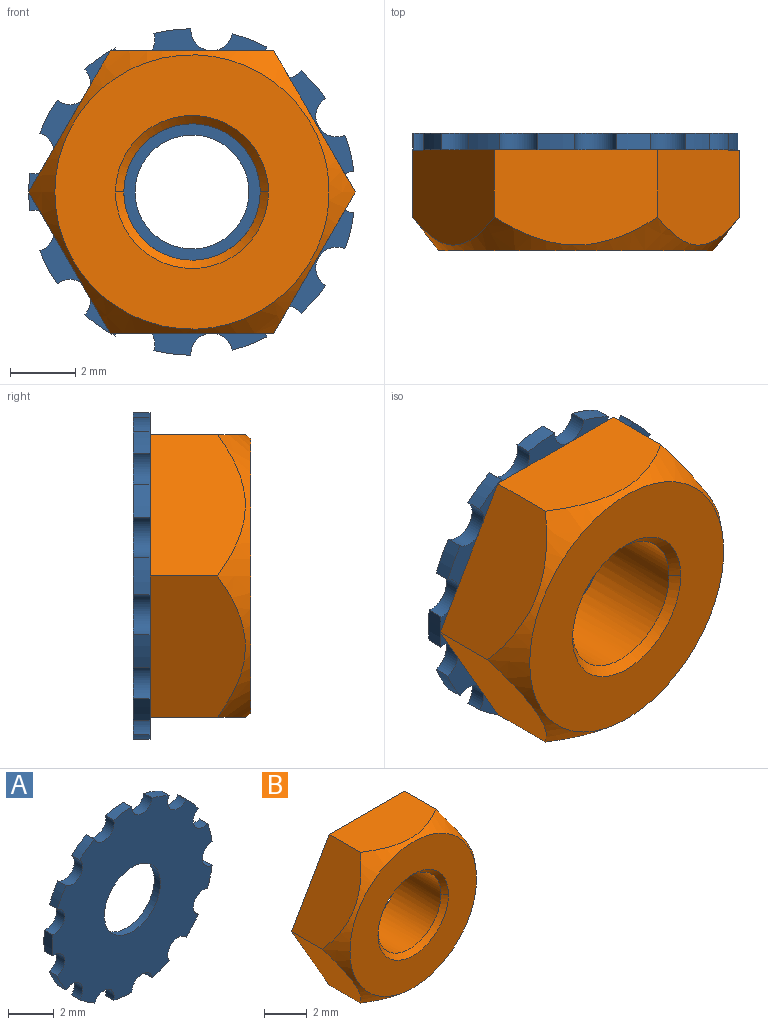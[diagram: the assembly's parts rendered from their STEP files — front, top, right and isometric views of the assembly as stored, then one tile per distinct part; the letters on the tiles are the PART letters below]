
ASSEMBLY  parts=2 mates=1
PART A: 31 faces, bbox 9.9x0.5x10 mm
  f0: cylinder r=4.99mm len=1.13mm, axis (0,1,0), area 0.6mm2, adj f1,f2,f3,f4
  f1: cylinder r=0.64mm len=1.26mm, axis (0,1,0), area 1mm2, adj f0,f2,f4,f19
  f2: plane 9.97x9.93mm, normal (0,1,0), area 43.3mm2, adj f0,f1,f3,f5,f6,f7,f8,f9
  f3: cylinder r=0.64mm len=1.21mm, axis (0,1,0), area 1mm2, adj f0,f2,f4,f15
  f4: plane 9.97x9.93mm, normal (0,-1,0), area 60.6mm2, adj f0,f1,f3,f5,f6,f7,f8,f9
  f5: cylinder r=4.99mm len=1.14mm, axis (0,1,0), area 0.6mm2, adj f2,f4,f23,f24
  f6: cylinder r=0.64mm len=1.27mm, axis (0,1,0), area 1mm2, adj f2,f4,f21,f25
  f7: cylinder r=4.99mm len=1.06mm, axis (0,1,0), area 0.6mm2, adj f2,f4,f12,f20
  f8: cylinder r=4.99mm len=0.85mm, axis (0,1,0), area 0.6mm2, adj f2,f4,f9,f16
  f9: cylinder r=0.64mm len=1.18mm, axis (0,1,0), area 1mm2, adj f2,f4,f8,f25
  f10: cylinder r=2.92mm len=5.84mm, axis (0,1,0), area 2.3mm2, adj f2,f30
  f11: cylinder r=4.99mm len=1.01mm, axis (0,1,0), area 0.6mm2, adj f2,f4,f23,f28
  f12: cylinder r=0.64mm len=1.13mm, axis (0,1,0), area 1mm2, adj f2,f4,f7,f14
  f13: cylinder r=0.64mm len=1.18mm, axis (0,1,0), area 1mm2, adj f2,f4,f14,f21
  f14: cylinder r=4.99mm len=0.85mm, axis (0,1,0), area 0.6mm2, adj f2,f4,f12,f13
  f15: cylinder r=4.99mm len=0.94mm, axis (0,1,0), area 0.6mm2, adj f2,f3,f4,f28
  f16: cylinder r=0.64mm len=1.13mm, axis (0,1,0), area 1mm2, adj f2,f4,f8,f19
  f17: cylinder r=4.99mm len=1.13mm, axis (0,1,0), area 0.6mm2, adj f2,f4,f20,f27
  f18: cylinder r=0.64mm len=1.08mm, axis (0,1,0), area 1mm2, adj f2,f4,f22,f26
  f19: cylinder r=4.99mm len=1.06mm, axis (0,1,0), area 0.6mm2, adj f1,f2,f4,f16
  f20: cylinder r=0.64mm len=1.26mm, axis (0,1,0), area 1mm2, adj f2,f4,f7,f17
  f21: cylinder r=4.99mm len=1.1mm, axis (0,1,0), area 0.6mm2, adj f2,f4,f6,f13
  f22: cylinder r=4.99mm len=0.94mm, axis (0,1,0), area 0.6mm2, adj f2,f4,f18,f27
  f23: cylinder r=0.64mm len=1.24mm, axis (0,1,0), area 1mm2, adj f2,f4,f5,f11
  f24: cylinder r=0.64mm len=1.24mm, axis (0,1,0), area 1mm2, adj f2,f4,f5,f26
  f25: cylinder r=4.99mm len=1.1mm, axis (0,1,0), area 0.6mm2, adj f2,f4,f6,f9
  f26: cylinder r=4.99mm len=1.01mm, axis (0,1,0), area 0.6mm2, adj f2,f4,f18,f24
  f27: cylinder r=0.64mm len=1.21mm, axis (0,1,0), area 1mm2, adj f2,f4,f17,f22
  f28: cylinder r=0.64mm len=1.08mm, axis (0,1,0), area 1mm2, adj f2,f4,f11,f15
  f29: cylinder r=1.74mm len=3.48mm, axis (0,1,0), area 4.2mm2, adj f4,f30
  f30: plane 5.84x5.84mm, normal (0,1,0), area 17.3mm2, adj f10,f29
PART B: 12 faces, bbox 10x3.1x10 mm
  f0: plane 4.99x2.91mm, normal (0,0,-1), area 13.1mm2, adj f1,f2,f3,f4
  f1: plane 4.32x2.91mm, normal (0.87,0,-0.5), area 13.1mm2, adj f0,f2,f3,f5
  f2: plane 9.97x8.64mm, normal (0,1,0), area 51mm2, adj f0,f1,f4,f5,f6,f7,f8
  f3: cone r=4.19mm half-angle=38deg, axis (0,1,0), area 15.3mm2, adj f0,f1,f4,f5,f7,f8,f9
  f4: plane 4.32x2.91mm, normal (-0.87,0,-0.5), area 13mm2, adj f0,f2,f3,f7
  f5: plane 4.32x2.91mm, normal (0.87,0,0.5), area 13.1mm2, adj f1,f2,f3,f8
  f6: cylinder r=2.08mm len=4.17mm, axis (0,1,0), area 36.9mm2, adj f2,f10,f11
  f7: plane 4.32x2.91mm, normal (-0.87,0,0.5), area 13mm2, adj f2,f3,f4,f8
  f8: plane 4.99x2.91mm, normal (0,0,1), area 13mm2, adj f2,f3,f5,f7
  f9: plane 8.38x8.38mm, normal (0,-1,0), area 38mm2, adj f3,f10,f11
  f10: bspline ~4.67x2.59mm, area 2.5mm2, adj f6,f9,f11
  f11: bspline ~4.68x2.63mm, area 2.5mm2, adj f6,f9,f10
PLACE A t=(-0.05,4.06,2.52)mm
PLACE B t=(-0.05,4.06,2.52)mm
MATE fastened B.f3 <-> A.f0  axis (0,1,0) through (-15.63,4.06,5.63)mm
